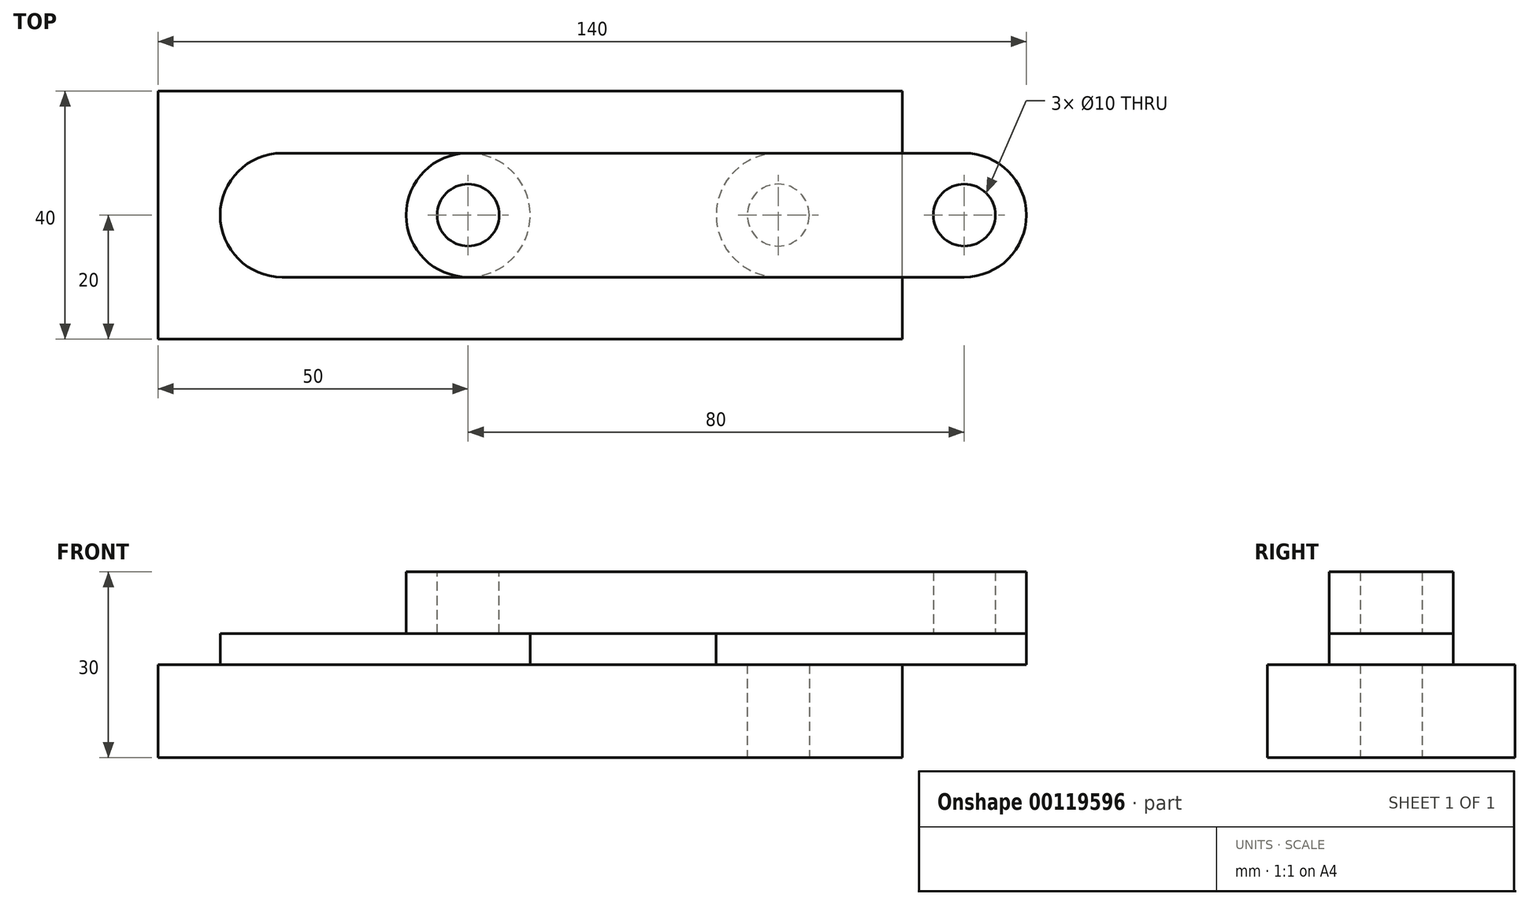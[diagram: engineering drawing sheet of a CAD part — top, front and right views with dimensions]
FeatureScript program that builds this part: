
annotation { "Feature Type Name" : "Feature", "Feature Type Description" : "" }
export const myFeature = defineFeature(function(context is Context, id is Id, definition is map)
    precondition{}
    {
        {
            var Q0;
            Q0=qCreatedBy(makeId("Top.planeOp"),FACE);
            var sketch = newSketch(context, id + "F0", { "sketchPlane" : qUnion([Q0])});
            skLineSegment(sketch, "E0.bottom", {"start": v(0, 0) * mm, "end": v(120, 0) * mm});
            skLineSegment(sketch, "E0.top", {"start": v(0, 40) * mm, "end": v(120, 40) * mm});
            skLineSegment(sketch, "E0.left", {"start": v(0, 0) * mm, "end": v(0, 40) * mm});
            skLineSegment(sketch, "E0.right", {"start": v(120, 0) * mm, "end": v(120, 40) * mm});
            skCircle(sketch, "E1", {"center": v(20, 20) * mm, "radius": 5 * mm});
            skCircle(sketch, "E2", {"center": v(100, 20) * mm, "radius": 5 * mm});
            skSolve(sketch);
        }
        {
            var Q0;
            Q0=makeQuery(id+"F0.imprint","IMPRINT",FACE,{"disambiguationData":[TD([[makeQuery(id+"F0.imprint","IMPRINT",EDGE,{"derivedFrom":sQuery(id+"F0.wireOp",EDGE,"E0.bottom")}),1.0]])]});
            extrude(context, id + "F1", {"entities" : qUnion([Q0]), "depth" : 15 * mm});
        }
        {
            var Q0;
            Q0=makeQuery(id+"F1.opExtrude","CAP_FACE",FACE,{"disambiguationData":[OSD([sQuery(id+"F0.wireOp",EDGE,"E0.bottom"),sQuery(id+"F0.wireOp",EDGE,"E0.top"),sQuery(id+"F0.wireOp",EDGE,"E0.left"),sQuery(id+"F0.wireOp",EDGE,"E0.right"),sQuery(id+"F0.wireOp",EDGE,"E1"),sQuery(id+"F0.wireOp",EDGE,"E2")])],"isStart":false});
            var sketch = newSketch(context, id + "F2", { "sketchPlane" : qUnion([Q0])});
            skCircle(sketch, "E3", {"center": v(20, 20) * mm, "radius": 5 * mm});
            skLineSegment(sketch, "E4", {"start": v(20, 10) * mm, "end": v(50, 10) * mm});
            skLineSegment(sketch, "E5", {"start": v(20, 30) * mm, "end": v(50, 30) * mm});
            skArc(sketch, "E6", {"start": v(20, 30) * mm, "mid": v(10, 20) * mm, "end": v(20, 10) * mm});
            skArc(sketch, "E7", {"start": v(50, 10) * mm, "mid": v(60, 20) * mm, "end": v(50, 30) * mm});
            skSolve(sketch);
        }
        {
            var Q0;
            Q0=makeQuery(id+"F2.imprint","IMPRINT",FACE,{"disambiguationData":[TD([[makeQuery(id+"F2.imprint","IMPRINT",EDGE,{"derivedFrom":sQuery(id+"F2.wireOp",EDGE,"E4")}),-1.0]])]});
            var sketch = newSketch(context, id + "F3", { "sketchPlane" : qUnion([Q0])});
            skSolve(sketch);
        }
        {
            var Q0;
            Q0=makeQuery(id+"F3.imprint","IMPRINT",FACE,{"disambiguationData":[TD([[makeQuery(id+"F3.imprint","IMPRINT",EDGE,{"derivedFrom":makeQuery(id+"F2.imprint","IMPRINT",EDGE,{"derivedFrom":sQuery(id+"F2.wireOp",EDGE,"E4")})}),1.0]])]});
            extrude(context, id + "F4", {"entities" : qUnion([Q0]), "depth" : 5 * mm});
        }
        {
            var Q0;
            Q0=makeQuery(id+"F4.opExtrude","CAP_FACE",FACE,{"disambiguationData":[OSD([sQuery(id+"F2.wireOp",EDGE,"E4"),sQuery(id+"F2.wireOp",EDGE,"E5"),sQuery(id+"F2.wireOp",EDGE,"E6"),sQuery(id+"F2.wireOp",EDGE,"E7")])],"isStart":false});
            var sketch = newSketch(context, id + "F5", { "sketchPlane" : qUnion([Q0])});
            skCircle(sketch, "E8", {"center": v(50, 20) * mm, "radius": 5 * mm});
            skSolve(sketch);
        }
        {
            var Q0;
            Q0=makeQuery(id+"F5.imprint","IMPRINT",FACE,{"disambiguationData":[TD([[makeQuery(id+"F5.imprint","IMPRINT",EDGE,{"derivedFrom":sQuery(id+"F5.wireOp",EDGE,"E8")}),1.0]])]});
            extrude(context, id + "F6", {"entities" : qUnion([Q0]), "operationType" : NewBodyOperationType.ADD, "depth" : 10 * mm});
        }
        {
            var Q0;
            Q0=makeQuery(id+"F0.imprint","IMPRINT",FACE,{"disambiguationData":[TD([[makeQuery(id+"F0.imprint","IMPRINT",EDGE,{"derivedFrom":sQuery(id+"F0.wireOp",EDGE,"E1")}),1.0]])]});
            var Q1;
            Q1=makeQuery(id+"F4.opExtrude","CAP_FACE",FACE,{"disambiguationData":[OSD([sQuery(id+"F2.wireOp",EDGE,"E4"),sQuery(id+"F2.wireOp",EDGE,"E5"),sQuery(id+"F2.wireOp",EDGE,"E6"),sQuery(id+"F2.wireOp",EDGE,"E7")])],"isStart":true});
            extrude(context, id + "F7", {"entities" : qUnion([Q0]), "operationType" : NewBodyOperationType.ADD, "endBound" : BoundingType.UP_TO_SURFACE, "endBoundEntityFace" : qUnion([Q1]), "depth" : 25 * mm});
        }
        {
            var Q0;
            Q0=makeQuery(id+"F2.imprint","IMPRINT",FACE,{"disambiguationData":[TD([[makeQuery(id+"F2.imprint","IMPRINT",EDGE,{"derivedFrom":makeQuery(id+"F1.opExtrude","CAP_EDGE",EDGE,{"disambiguationData":[OSD([sQuery(id+"F0.wireOp",EDGE,"E2")])],"isStart":false})}),1.0]])]});
            var sketch = newSketch(context, id + "F8", { "sketchPlane" : qUnion([Q0])});
            skLineSegment(sketch, "E9", {"start": v(100, 10) * mm, "end": v(130, 10) * mm});
            skLineSegment(sketch, "E10", {"start": v(100, 30) * mm, "end": v(130, 30) * mm});
            skArc(sketch, "E11", {"start": v(100, 30) * mm, "mid": v(90, 20) * mm, "end": v(100, 10) * mm});
            skArc(sketch, "E12", {"start": v(130, 10) * mm, "mid": v(140, 20) * mm, "end": v(130, 30) * mm});
            skSolve(sketch);
        }
        {
            var Q0;
            Q0=makeQuery(id+"F8.imprint","IMPRINT",FACE,{"disambiguationData":[TD([[makeQuery(id+"F8.imprint","IMPRINT",EDGE,{"derivedFrom":sQuery(id+"F8.wireOp",EDGE,"E9")}),1.0]])]});
            var Q1;
            Q1=makeQuery(id+"F8.imprint","IMPRINT",FACE,{"disambiguationData":[TD([[makeQuery(id+"F8.imprint","IMPRINT",EDGE,{"derivedFrom":makeQuery(id+"F2.imprint","IMPRINT",EDGE,{"derivedFrom":makeQuery(id+"F1.opExtrude","CAP_EDGE",EDGE,{"disambiguationData":[OSD([sQuery(id+"F0.wireOp",EDGE,"E2")])],"isStart":false})})}),1.0]])]});
            extrude(context, id + "F9", {"entities" : qUnion([Q0, Q1]), "depth" : 5 * mm});
        }
        {
            var Q0;
            Q0=makeQuery(id+"F9.opExtrude","CAP_FACE",FACE,{"disambiguationData":[OSD([sQuery(id+"F8.wireOp",EDGE,"E9"),sQuery(id+"F8.wireOp",EDGE,"E10"),sQuery(id+"F8.wireOp",EDGE,"E11"),sQuery(id+"F8.wireOp",EDGE,"E12")])],"isStart":false});
            var sketch = newSketch(context, id + "F10", { "sketchPlane" : qUnion([Q0])});
            skCircle(sketch, "E13", {"center": v(130, 20) * mm, "radius": 5 * mm});
            skSolve(sketch);
        }
        {
            var Q0;
            Q0=makeQuery(id+"F10.imprint","IMPRINT",FACE,{"disambiguationData":[TD([[makeQuery(id+"F10.imprint","IMPRINT",EDGE,{"derivedFrom":sQuery(id+"F10.wireOp",EDGE,"E13")}),1.0]])]});
            extrude(context, id + "F11", {"entities" : qUnion([Q0]), "operationType" : NewBodyOperationType.ADD, "depth" : 10 * mm});
        }
        {
            var Q0;
            Q0=makeQuery(id+"F0.imprint","IMPRINT",FACE,{"disambiguationData":[TD([[makeQuery(id+"F0.imprint","IMPRINT",EDGE,{"derivedFrom":sQuery(id+"F0.wireOp",EDGE,"E2")}),1.0]])]});
            extrude(context, id + "F12", {"entities" : qUnion([Q0]), "endBound" : BoundingType.UP_TO_NEXT, "depth" : 10 * mm});
        }
        {
            var Q0;
            Q0=makeQuery(id+"F6.opExtrude","CAP_FACE",FACE,{"disambiguationData":[OSD([sQuery(id+"F5.wireOp",EDGE,"E8")])],"isStart":false});
            var sketch = newSketch(context, id + "F13", { "sketchPlane" : qUnion([Q0])});
            skCircle(sketch, "E14", {"center": v(50, 20) * mm, "radius": 5 * mm});
            skCircle(sketch, "E15", {"center": v(130, 20) * mm, "radius": 5 * mm});
            skLineSegment(sketch, "E16", {"start": v(50, 30) * mm, "end": v(130, 30) * mm});
            skLineSegment(sketch, "E17", {"start": v(50, 10) * mm, "end": v(130, 10) * mm});
            skArc(sketch, "E18", {"start": v(50, 30) * mm, "mid": v(40, 20) * mm, "end": v(50, 10) * mm});
            skArc(sketch, "E19", {"start": v(130, 10) * mm, "mid": v(140, 20) * mm, "end": v(130, 30) * mm});
            skSolve(sketch);
        }
        {
            var Q0;
            Q0=makeQuery(id+"F13.imprint","IMPRINT",FACE,{"disambiguationData":[TD([[makeQuery(id+"F13.imprint","IMPRINT",EDGE,{"derivedFrom":sQuery(id+"F13.wireOp",EDGE,"E14")}),-1.0]])]});
            extrude(context, id + "F14", {"entities" : qUnion([Q0]), "oppositeDirection" : true, "depth" : 10 * mm});
        }
    });
